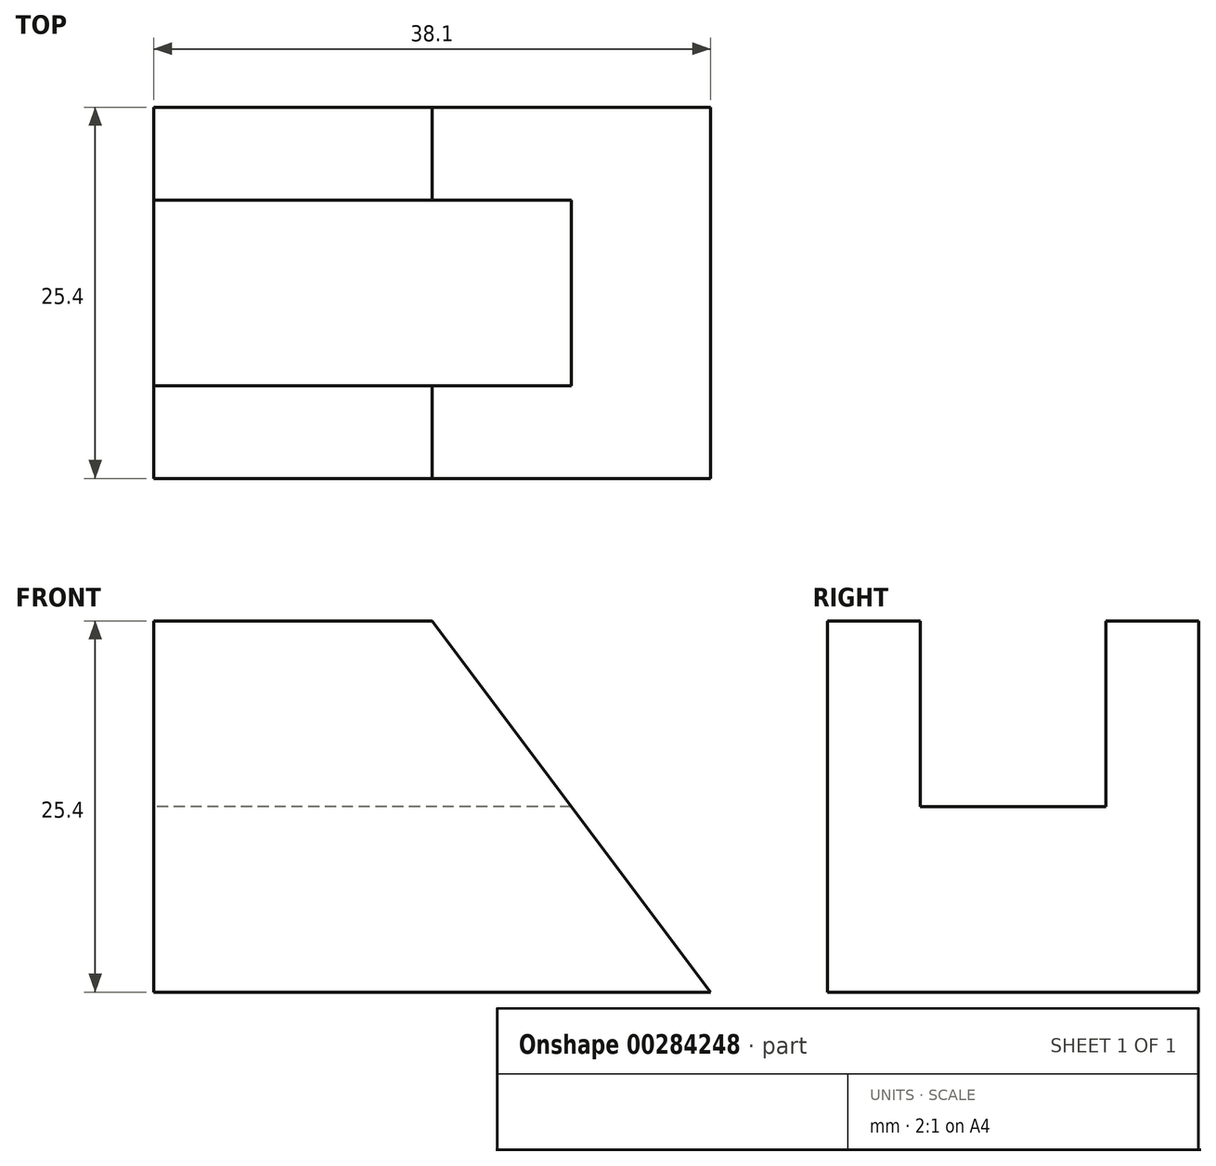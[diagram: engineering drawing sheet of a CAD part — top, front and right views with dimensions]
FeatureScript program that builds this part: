
annotation { "Feature Type Name" : "Feature", "Feature Type Description" : "" }
export const myFeature = defineFeature(function(context is Context, id is Id, definition is map)
    precondition{}
    {
        {
            var Q0;
            Q0=qCreatedBy(makeId("Front.planeOp"),FACE);
            var sketch = newSketch(context, id + "F0", { "sketchPlane" : qUnion([Q0])});
            skLineSegment(sketch, "E0", {"start": v(0, 0) * mm, "end": v(0, 25.4) * mm});
            skLineSegment(sketch, "E1", {"start": v(0, 25.4) * mm, "end": v(19.05, 25.4) * mm});
            skLineSegment(sketch, "E2", {"start": v(0, 0) * mm, "end": v(38.1, 0) * mm});
            skLineSegment(sketch, "E3", {"start": v(38.1, 0) * mm, "end": v(19.05, 25.4) * mm});
            skSolve(sketch);
        }
        {
            var Q0;
            Q0 = qSketchRegion(id + "F0", true);
            extrude(context, id + "F1", {"entities" : qUnion([Q0]), "depth" : 25.4 * mm});
        }
        {
            var Q0;
            Q0=qCreatedBy(makeId("Right.planeOp"),FACE);
            var sketch = newSketch(context, id + "F2", { "sketchPlane" : qUnion([Q0])});
            skLineSegment(sketch, "E4", {"start": v(-6.35, 25.4) * mm, "end": v(-6.35, 12.7) * mm});
            skLineSegment(sketch, "E5", {"start": v(-19.05, 25.4) * mm, "end": v(-19.05, 12.7) * mm});
            skLineSegment(sketch, "E6", {"start": v(-19.05, 25.4) * mm, "end": v(-6.35, 25.4) * mm});
            skLineSegment(sketch, "E7", {"start": v(-6.35, 12.7) * mm, "end": v(-19.05, 12.7) * mm});
            skSolve(sketch);
        }
        {
            var Q0;
            Q0 = qSketchRegion(id + "F2", true);
            extrude(context, id + "F3", {"entities" : qUnion([Q0]), "operationType" : NewBodyOperationType.REMOVE, "endBound" : BoundingType.THROUGH_ALL, "depth" : 25.4 * mm});
        }
    });
